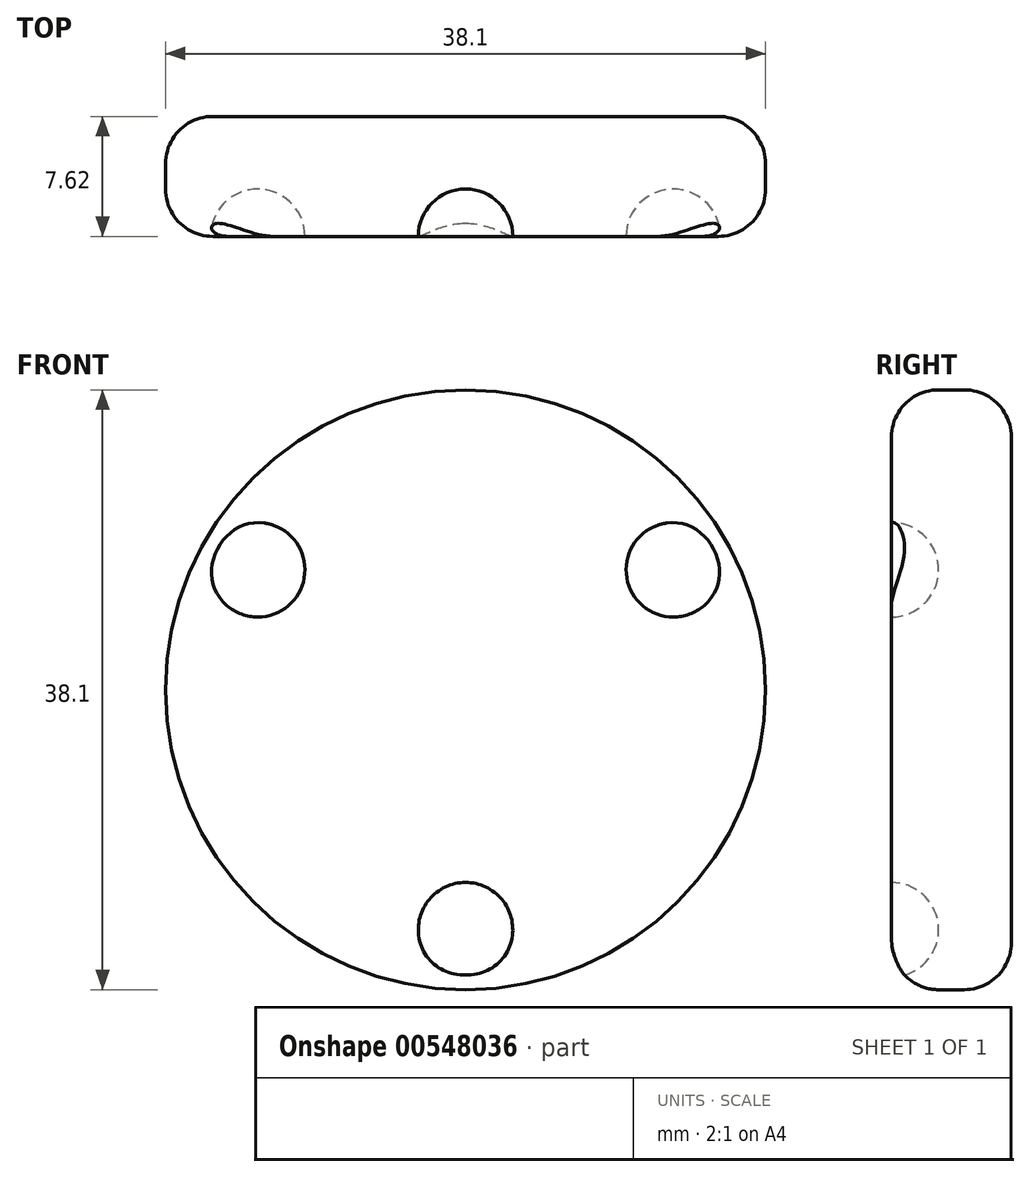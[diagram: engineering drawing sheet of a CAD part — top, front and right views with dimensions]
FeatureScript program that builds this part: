
annotation { "Feature Type Name" : "Feature", "Feature Type Description" : "" }
export const myFeature = defineFeature(function(context is Context, id is Id, definition is map)
    precondition{}
    {
        {
            var Q0;
            Q0=qCreatedBy(makeId("Front.planeOp"),FACE);
            var sketch = newSketch(context, id + "F0", { "sketchPlane" : qUnion([Q0])});
            skCircle(sketch, "E0", {"center": v(0, 0) * mm, "radius": 19.05 * mm});
            skSolve(sketch);
        }
        {
            var Q0;
            Q0=makeQuery(id+"F0.imprint","IMPRINT",FACE,{"disambiguationData":[TD([[makeQuery(id+"F0.imprint","IMPRINT",EDGE,{"derivedFrom":sQuery(id+"F0.wireOp",EDGE,"E0")}),1.0]])]});
            extrude(context, id + "F1", {"entities" : qUnion([Q0]), "depth" : 7.62 * mm, "offsetDistance" : 25.4 * mm});
        }
        {
            var Q0;
            Q0=makeQuery(id+"F1.opExtrude","CAP_FACE",FACE,{"disambiguationData":[OSD([sQuery(id+"F0.wireOp",EDGE,"E0")])],"isStart":false});
            var sketch = newSketch(context, id + "F2", { "sketchPlane" : qUnion([Q0])});
            skCircle(sketch, "E1.cCircle", {"center": v(0, 0) * mm, "radius": 7.62 * mm, "construction": true});
            skLineSegment(sketch, "E1.0", {"start": v(-13.2, 7.62) * mm, "end": v(13.2, 7.62) * mm, "construction": true});
            skLineSegment(sketch, "E1.1", {"start": v(13.2, 7.62) * mm, "end": v(0, -15.24) * mm, "construction": true});
            skLineSegment(sketch, "E1.2", {"start": v(0, -15.24) * mm, "end": v(-13.2, 7.62) * mm, "construction": true});
            skPoint(sketch, "E1.0.midPoint", {"position": v(0, 7.62) * mm});
            skCircle(sketch, "E2", {"center": v(-13.2, 7.62) * mm, "radius": 3 * mm});
            skCircle(sketch, "E3", {"center": v(13.2, 7.62) * mm, "radius": 3 * mm});
            skCircle(sketch, "E4", {"center": v(0, -15.24) * mm, "radius": 3 * mm});
            skLineSegment(sketch, "E5", {"start": v(-13.2, 2.61) * mm, "end": v(-13.2, 12.04) * mm});
            skLineSegment(sketch, "E6", {"start": v(13.2, 13.74) * mm, "end": v(13.2, 1.09) * mm});
            skLineSegment(sketch, "E7", {"start": v(0, -10.5) * mm, "end": v(0, -20.91) * mm});
            skSolve(sketch);
        }
        {
            var Q0;
            {var subQ0=sQuery(id+"F2.wireOp",EDGE,"E5");var subQ1=sQuery(id+"F2.wireOp",EDGE,"E2");var subQ2=makeQuery(id+"F2.imprint","INTERSECT",VERTEX,{"disambiguationData":[OD(0.0)],"derivedFrom":[subQ1,subQ0]});Q0=makeQuery(id+"F2.imprint","IMPRINT",FACE,{"disambiguationData":[TD([[makeQuery(id+"F2.imprint","IMPRINT",EDGE,{"disambiguationData":[TD([[subQ2,1.0]])],"derivedFrom":subQ1}),1.0]])]});}
            var Q1;
            Q1=sQuery(id+"F2.wireOp",EDGE,"E5");
            revolve(context, id + "F3", {"operationType" : NewBodyOperationType.ADD, "entities" : qUnion([Q0]), "axis" : qUnion([Q1]), "revolveType" : RevolveType.FULL});
        }
        {
            var Q0;
            {var subQ0=sQuery(id+"F2.wireOp",EDGE,"E6");var subQ1=sQuery(id+"F2.wireOp",EDGE,"E3");var subQ2=makeQuery(id+"F2.imprint","INTERSECT",VERTEX,{"disambiguationData":[OD(0.0)],"derivedFrom":[subQ1,subQ0]});Q0=makeQuery(id+"F2.imprint","IMPRINT",FACE,{"disambiguationData":[TD([[makeQuery(id+"F2.imprint","IMPRINT",EDGE,{"disambiguationData":[TD([[subQ2,1.0]])],"derivedFrom":subQ1}),1.0]])]});}
            var Q1;
            Q1=sQuery(id+"F2.wireOp",EDGE,"E6");
            revolve(context, id + "F4", {"operationType" : NewBodyOperationType.ADD, "entities" : qUnion([Q0]), "axis" : qUnion([Q1]), "revolveType" : RevolveType.FULL});
        }
        {
            var Q0;
            {var subQ0=sQuery(id+"F2.wireOp",EDGE,"E7");var subQ1=sQuery(id+"F2.wireOp",EDGE,"E4");var subQ2=makeQuery(id+"F2.imprint","INTERSECT",VERTEX,{"disambiguationData":[OD(0.0)],"derivedFrom":[subQ1,subQ0]});Q0=makeQuery(id+"F2.imprint","IMPRINT",FACE,{"disambiguationData":[TD([[makeQuery(id+"F2.imprint","IMPRINT",EDGE,{"disambiguationData":[TD([[subQ2,1.0]])],"derivedFrom":subQ1}),1.0]])]});}
            var Q1;
            Q1=sQuery(id+"F2.wireOp",EDGE,"E7");
            revolve(context, id + "F5", {"operationType" : NewBodyOperationType.ADD, "entities" : qUnion([Q0]), "axis" : qUnion([Q1]), "revolveType" : RevolveType.FULL});
        }
        {
            var Q0;
            Q0=makeQuery(id+"F1.opExtrude","CAP_EDGE",EDGE,{"disambiguationData":[OSD([sQuery(id+"F0.wireOp",EDGE,"E0")])],"isStart":false});
            var Q1;
            Q1=makeQuery(id+"F1.opExtrude","CAP_EDGE",EDGE,{"disambiguationData":[OSD([sQuery(id+"F0.wireOp",EDGE,"E0")])],"isStart":true});
            fillet(context, id + "F6", {"entities" : qUnion([Q0, Q1]), "radius" : 3 * mm, "tangentPropagation" : true, "allowEdgeOverflow" : false});
        }
    });
